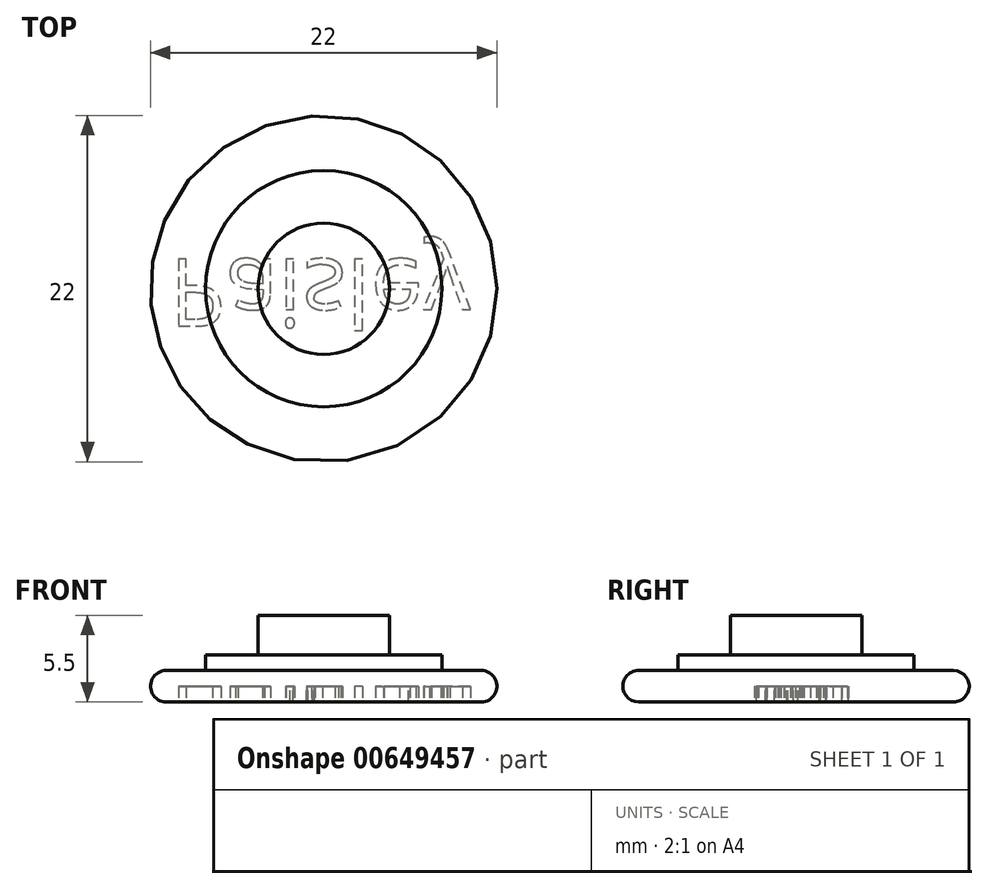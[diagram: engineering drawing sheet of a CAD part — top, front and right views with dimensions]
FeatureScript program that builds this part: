
annotation { "Feature Type Name" : "Feature", "Feature Type Description" : "" }
export const myFeature = defineFeature(function(context is Context, id is Id, definition is map)
    precondition{}
    {
        {
            var Q0;
            Q0=qCreatedBy(makeId("Top.planeOp"),FACE);
            var sketch = newSketch(context, id + "F0", { "sketchPlane" : qUnion([Q0])});
            skCircle(sketch, "E0", {"center": v(0, 0) * mm, "radius": 11 * mm});
            skCircle(sketch, "E1", {"center": v(0, 0) * mm, "radius": 7.5 * mm});
            skCircle(sketch, "E2", {"center": v(0, 0) * mm, "radius": 4.17 * mm});
            skSolve(sketch);
        }
        {
            var Q0;
            Q0=makeQuery(id+"F0.imprint","IMPRINT",FACE,{"disambiguationData":[TD([[makeQuery(id+"F0.imprint","IMPRINT",EDGE,{"derivedFrom":sQuery(id+"F0.wireOp",EDGE,"E0")}),1.0]])]});
            extrude(context, id + "F1", {"entities" : qUnion([Q0]), "depth" : 2 * mm, "offsetDistance" : 25 * mm});
        }
        {
            var Q0;
            Q0=makeQuery(id+"F0.imprint","IMPRINT",FACE,{"disambiguationData":[TD([[makeQuery(id+"F0.imprint","IMPRINT",EDGE,{"derivedFrom":sQuery(id+"F0.wireOp",EDGE,"E1")}),1.0]])]});
            extrude(context, id + "F2", {"entities" : qUnion([Q0]), "operationType" : NewBodyOperationType.ADD, "depth" : 3 * mm, "offsetDistance" : 25 * mm});
        }
        {
            var Q0;
            Q0=makeQuery(id+"F0.imprint","IMPRINT",FACE,{"disambiguationData":[TD([[makeQuery(id+"F0.imprint","IMPRINT",EDGE,{"derivedFrom":sQuery(id+"F0.wireOp",EDGE,"E2")}),1.0]])]});
            extrude(context, id + "F3", {"entities" : qUnion([Q0]), "operationType" : NewBodyOperationType.ADD, "depth" : 5.5 * mm, "offsetDistance" : 25 * mm});
        }
        {
            var Q0;
            Q0=makeQuery(id+"F1.opExtrude","CAP_EDGE",EDGE,{"disambiguationData":[OSD([sQuery(id+"F0.wireOp",EDGE,"E0")])],"isStart":false});
            var Q1;
            Q1=makeQuery(id+"F1.opExtrude","CAP_EDGE",EDGE,{"disambiguationData":[OSD([sQuery(id+"F0.wireOp",EDGE,"E0")])],"isStart":true});
            fillet(context, id + "F4", {"entities" : qUnion([Q0, Q1]), "radius" : 1 * mm, "tangentPropagation" : true, "allowEdgeOverflow" : false});
        }
        {
            var Q0;
            {var subQ0=sQuery(id+"F0.wireOp",EDGE,"E2");var subQ1=sQuery(id+"F0.wireOp",EDGE,"E1");Q0=makeQuery(id+"F3.boolean.opBoolean","MERGE",FACE,{"derivedFrom":[makeQuery(id+"F2.boolean.opBoolean","MERGE",FACE,{"derivedFrom":[makeQuery(id+"F1.opExtrude","CAP_FACE",FACE,{"disambiguationData":[OSD([sQuery(id+"F0.wireOp",EDGE,"E0"),subQ1])],"isStart":true}),makeQuery(id+"F2.opExtrude","CAP_FACE",FACE,{"disambiguationData":[OSD([subQ1,subQ0])],"isStart":true})]}),makeQuery(id+"F3.opExtrude","CAP_FACE",FACE,{"disambiguationData":[OSD([subQ0])],"isStart":true})]});}
            var sketch = newSketch(context, id + "F5", { "sketchPlane" : qUnion([Q0])});
            skText(sketch, "E3", { "text": "Paisley", "fontName": "OpenSans-Regular.ttf"});
            const initialGuessF5  = {"E3": [-0.00982, -0.00188, 1, 0, 0.0043]};
            skSetInitialGuess(sketch, initialGuessF5);
            skSolve(sketch);
        }
        {
            var Q0;
            Q0 = qSketchRegion(id + "F5", true);
            extrude(context, id + "F6", {"entities" : qUnion([Q0]), "operationType" : NewBodyOperationType.REMOVE, "oppositeDirection" : true, "depth" : 1 * mm, "offsetDistance" : 25 * mm});
        }
    });
